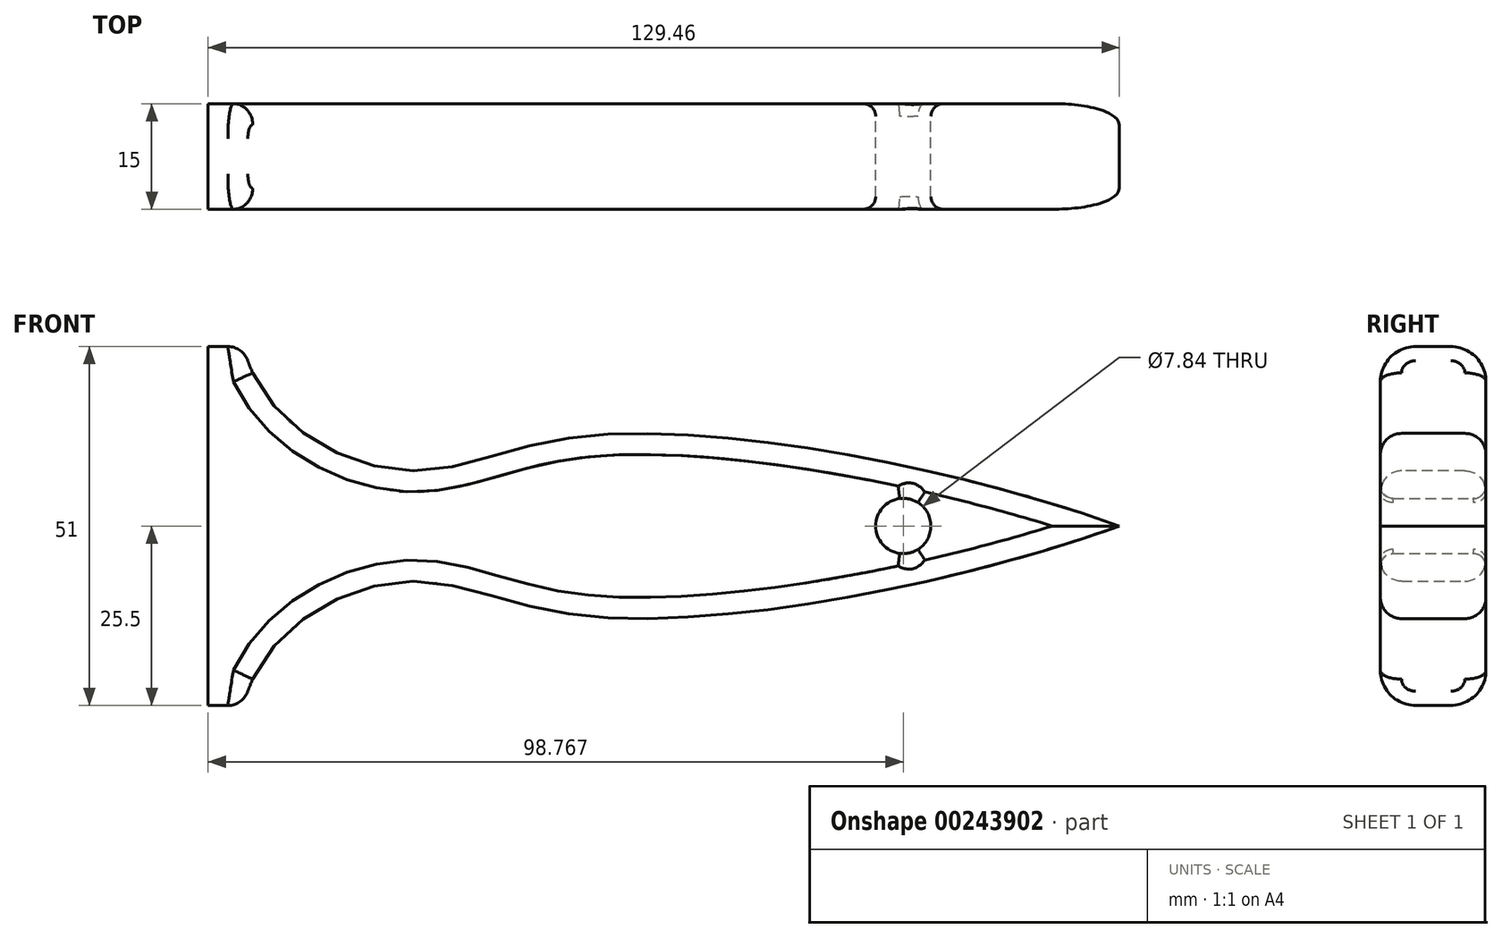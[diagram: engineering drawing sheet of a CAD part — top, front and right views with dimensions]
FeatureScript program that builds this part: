
annotation { "Feature Type Name" : "Feature", "Feature Type Description" : "" }
export const myFeature = defineFeature(function(context is Context, id is Id, definition is map)
    precondition{}
    {
        {
            var Q0;
            Q0=qCreatedBy(makeId("Front.planeOp"),FACE);
            var sketch = newSketch(context, id + "F0", { "sketchPlane" : qUnion([Q0])});
            skLineSegment(sketch, "E0.right", {"start": v(-64.73, -25.5) * mm, "end": v(-64.73, 25.5) * mm});
            skPoint(sketch, "E0.middle", {"position": v(0, 0) * mm});
            skFitSpline(sketch, "E1", {"points": [v(-59.66, 25.5) * mm, v(-37.25, 7.92) * mm, v(-12.41, 12.65) * mm, v(64.73, 0) * mm], "startDerivative": vector(26.12, -116.2) * mm, "endDerivative": vector(160.12, -57.33) * mm});
            skFitSpline(sketch, "E2.MirrorCS", {"points": [v(-59.66, -25.5) * mm, v(-37.25, -7.92) * mm, v(-12.41, -12.65) * mm, v(64.73, 0) * mm], "startDerivative": vector(26.12, 116.2) * mm, "endDerivative": vector(160.12, 57.33) * mm});
            skLineSegment(sketch, "E3", {"start": v(-59.66, 25.5) * mm, "end": v(-64.73, 25.5) * mm});
            skLineSegment(sketch, "E4", {"start": v(-64.73, -25.5) * mm, "end": v(-59.66, -25.5) * mm});
            skSolve(sketch);
        }
        {
            var Q0;
            Q0=makeQuery(id+"F0.imprint","IMPRINT",FACE,{"disambiguationData":[TD([[makeQuery(id+"F0.imprint","IMPRINT",EDGE,{"derivedFrom":sQuery(id+"F0.wireOp",EDGE,"E0.right")}),-1.0]])]});
            extrude(context, id + "F1", {"entities" : qUnion([Q0]), "endBound" : BoundingType.SYMMETRIC, "depth" : 15 * mm});
        }
        {
            var Q0;
            Q0=makeQuery(id+"F1.opExtrude","CAP_EDGE",EDGE,{"disambiguationData":[OSD([sQuery(id+"F0.wireOp",EDGE,"E4")])],"isStart":false});
            var Q1;
            Q1=makeQuery(id+"F1.opExtrude","CAP_EDGE",EDGE,{"disambiguationData":[OSD([sQuery(id+"F0.wireOp",EDGE,"E4")])],"isStart":true});
            var Q2;
            Q2=makeQuery(id+"F1.opExtrude","CAP_EDGE",EDGE,{"disambiguationData":[OSD([sQuery(id+"F0.wireOp",EDGE,"E3")])],"isStart":false});
            var Q3;
            Q3=makeQuery(id+"F1.opExtrude","CAP_EDGE",EDGE,{"disambiguationData":[OSD([sQuery(id+"F0.wireOp",EDGE,"E3")])],"isStart":true});
            fillet(context, id + "F2", {"entities" : qUnion([Q0, Q1, Q2, Q3]), "radius" : 5 * mm, "tangentPropagation" : true, "allowEdgeOverflow" : false});
        }
        {
            var Q0;
            Q0=makeQuery(id+"F1.opExtrude","CAP_EDGE",EDGE,{"disambiguationData":[OSD([sQuery(id+"F0.wireOp",EDGE,"E1")])],"isStart":false});
            var Q1;
            Q1=makeQuery(id+"F1.opExtrude","CAP_EDGE",EDGE,{"disambiguationData":[OSD([sQuery(id+"F0.wireOp",EDGE,"E2.MirrorCS")])],"isStart":false});
            fillet(context, id + "F3", {"entities" : qUnion([Q0, Q1]), "radius" : 3 * mm, "tangentPropagation" : true, "allowEdgeOverflow" : false});
        }
        {
            var Q0;
            Q0=qCreatedBy(makeId("Front.planeOp"),FACE);
            var sketch = newSketch(context, id + "F4", { "sketchPlane" : qUnion([Q0])});
            skCircle(sketch, "E5", {"center": v(34.04, 0) * mm, "radius": 3.92 * mm});
            skSolve(sketch);
        }
        {
            var Q0;
            Q0 = qSketchRegion(id + "F4", true);
            extrude(context, id + "F5", {"entities" : qUnion([Q0]), "operationType" : NewBodyOperationType.REMOVE, "endBound" : BoundingType.SYMMETRIC, "depth" : 25 * mm});
        }
        {
            var Q0;
            Q0=makeQuery(id+"F5.boolean.opBoolean","INTERSECT",EDGE,{"derivedFrom":[makeQuery(id+"F1.opExtrude","CAP_FACE",FACE,{"disambiguationData":[OSD([sQuery(id+"F0.wireOp",EDGE,"E0.right"),sQuery(id+"F0.wireOp",EDGE,"E1"),sQuery(id+"F0.wireOp",EDGE,"E2.MirrorCS"),sQuery(id+"F0.wireOp",EDGE,"E3"),sQuery(id+"F0.wireOp",EDGE,"E4")])],"isStart":true}),makeQuery(id+"F5.opExtrude","SWEPT_FACE",FACE,{"disambiguationData":[OSD([sQuery(id+"F4.wireOp",EDGE,"E5")])]})]});
            var Q1;
            Q1=makeQuery(id+"F5.boolean.opBoolean","INTERSECT",EDGE,{"derivedFrom":[makeQuery(id+"F1.opExtrude","CAP_FACE",FACE,{"disambiguationData":[OSD([sQuery(id+"F0.wireOp",EDGE,"E0.right"),sQuery(id+"F0.wireOp",EDGE,"E1"),sQuery(id+"F0.wireOp",EDGE,"E2.MirrorCS"),sQuery(id+"F0.wireOp",EDGE,"E3"),sQuery(id+"F0.wireOp",EDGE,"E4")])],"isStart":false}),makeQuery(id+"F5.opExtrude","SWEPT_FACE",FACE,{"disambiguationData":[OSD([sQuery(id+"F4.wireOp",EDGE,"E5")])]})]});
            fillet(context, id + "F6", {"entities" : qUnion([Q0, Q1]), "radius" : 1.8 * mm, "tangentPropagation" : true, "allowEdgeOverflow" : false});
        }
    });
